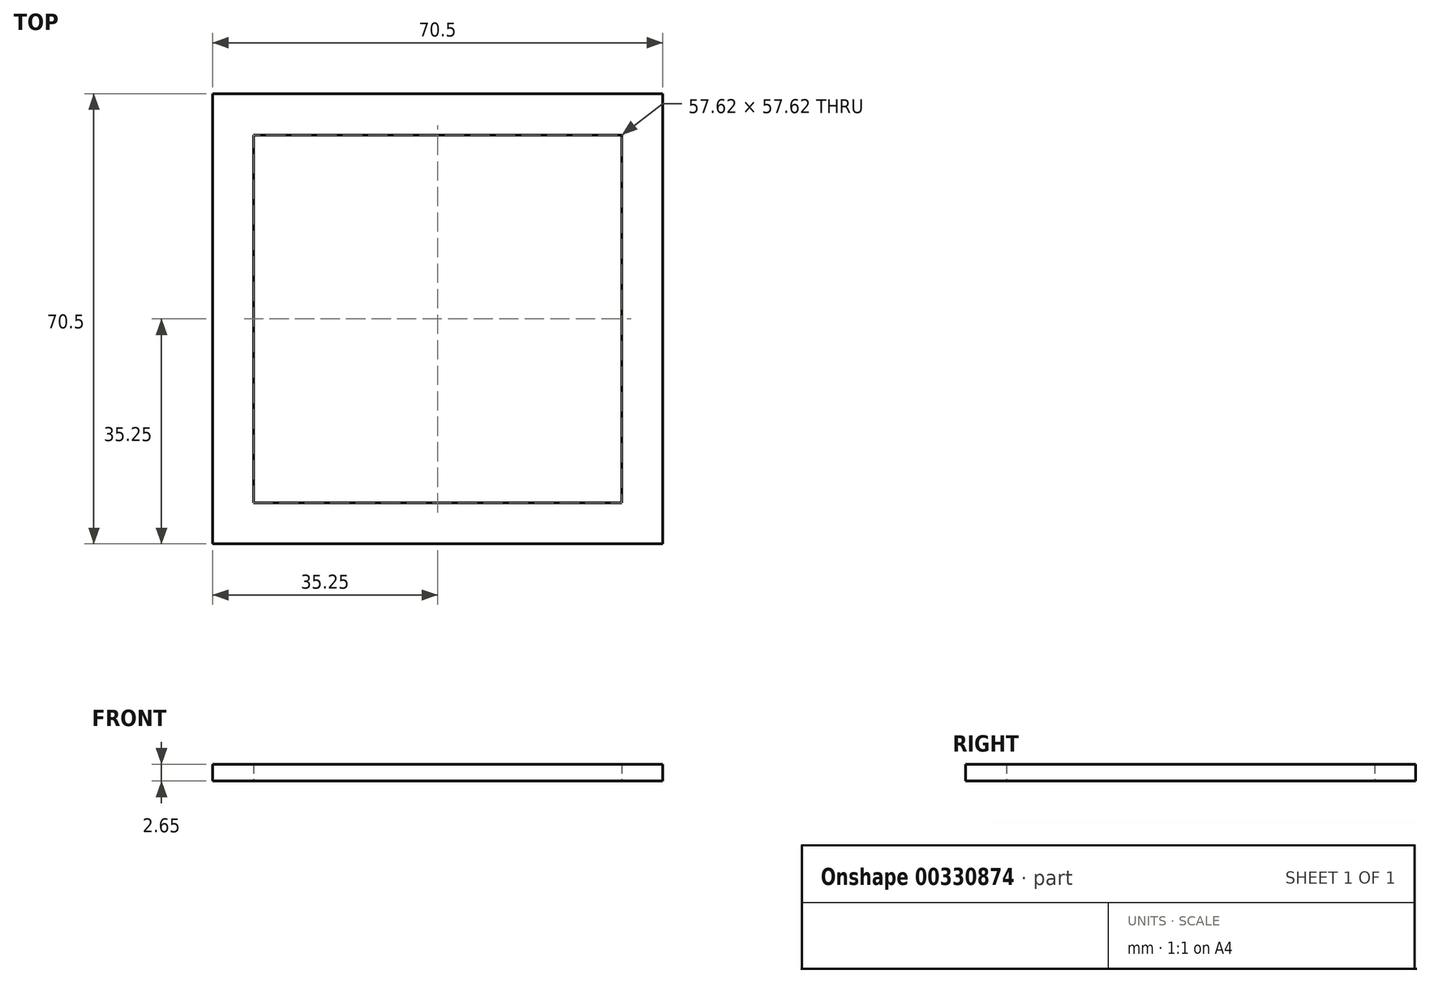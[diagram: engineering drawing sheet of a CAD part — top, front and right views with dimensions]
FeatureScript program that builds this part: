
annotation { "Feature Type Name" : "Feature", "Feature Type Description" : "" }
export const myFeature = defineFeature(function(context is Context, id is Id, definition is map)
    precondition{}
    {
        {
            var Q0;
            Q0=qCreatedBy(makeId("Top.planeOp"),FACE);
            var sketch = newSketch(context, id + "F0", { "sketchPlane" : qUnion([Q0])});
            skLineSegment(sketch, "E0.bottom", {"start": v(0, 0) * mm, "end": v(70.5, 0) * mm});
            skLineSegment(sketch, "E0.top", {"start": v(0, 70.5) * mm, "end": v(70.5, 70.5) * mm});
            skLineSegment(sketch, "E0.left", {"start": v(0, 0) * mm, "end": v(0, 70.5) * mm});
            skLineSegment(sketch, "E0.right", {"start": v(70.5, 0) * mm, "end": v(70.5, 70.5) * mm});
            skLineSegment(sketch, "E1", {"start": v(70.5, 70.5) * mm, "end": v(0, 0) * mm, "construction": true});
            skLineSegment(sketch, "E2", {"start": v(0, 70.5) * mm, "end": v(70.5, 0) * mm, "construction": true});
            skLineSegment(sketch, "E3.bottom", {"start": v(64.06, 6.44) * mm, "end": v(6.44, 6.44) * mm});
            skLineSegment(sketch, "E3.top", {"start": v(64.06, 64.06) * mm, "end": v(6.44, 64.06) * mm});
            skLineSegment(sketch, "E3.left", {"start": v(64.06, 6.44) * mm, "end": v(64.06, 64.06) * mm});
            skLineSegment(sketch, "E3.right", {"start": v(6.44, 6.44) * mm, "end": v(6.44, 64.06) * mm});
            skPoint(sketch, "E3.middle", {"position": v(35.25, 35.25) * mm});
            skSolve(sketch);
        }
        {
            var Q0;
            Q0=makeQuery(id+"F0.imprint","IMPRINT",FACE,{"disambiguationData":[TD([[makeQuery(id+"F0.imprint","IMPRINT",EDGE,{"derivedFrom":sQuery(id+"F0.wireOp",EDGE,"E0.bottom")}),1.0]])]});
            extrude(context, id + "F1", {"entities" : qUnion([Q0]), "depth" : 2.65 * mm});
        }
    });
